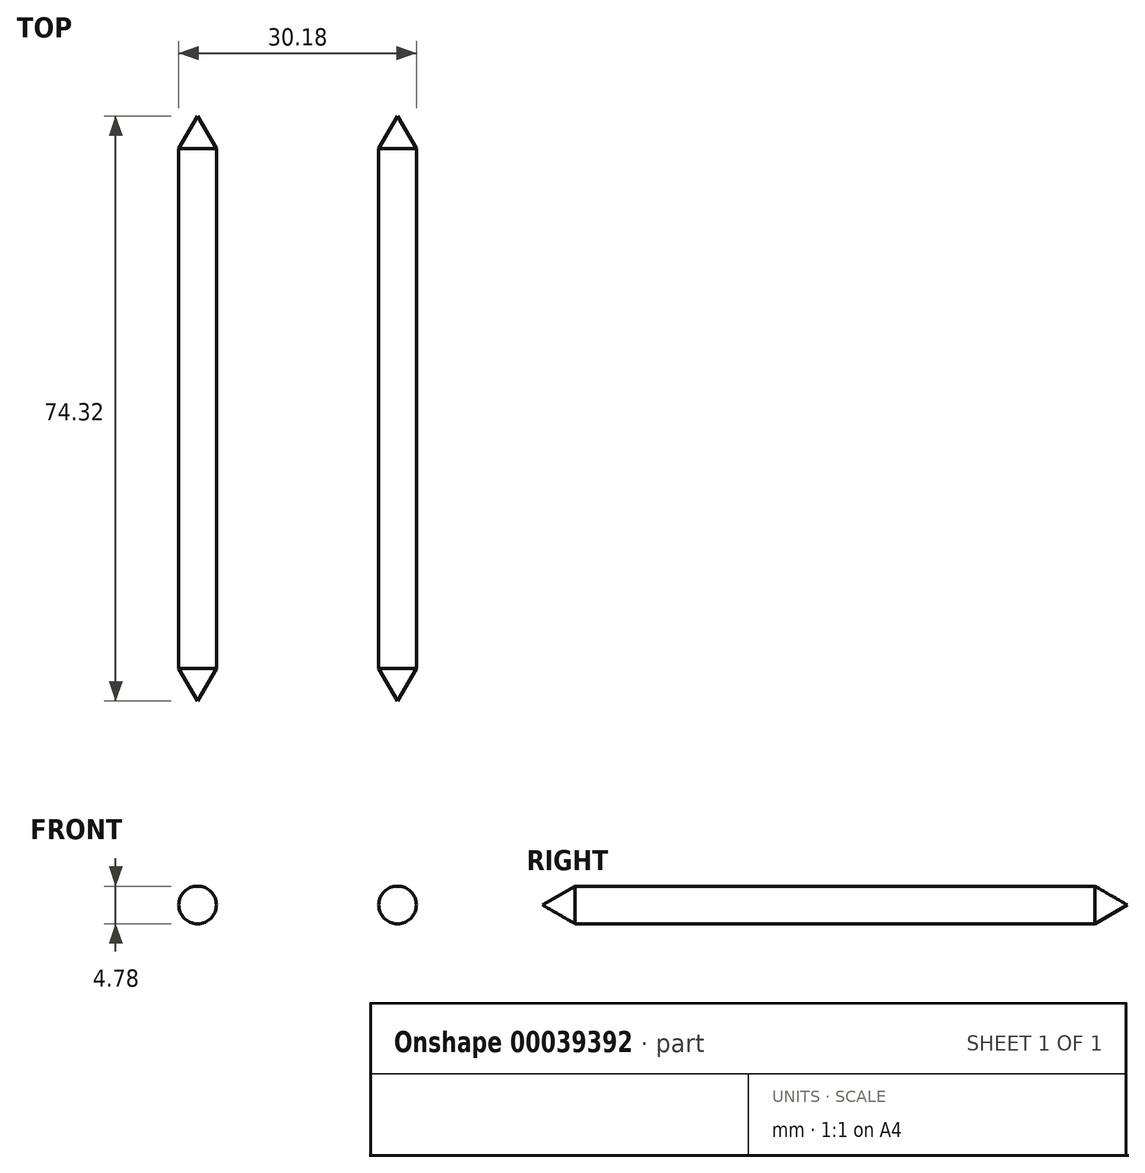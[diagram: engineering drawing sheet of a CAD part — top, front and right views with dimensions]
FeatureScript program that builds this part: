
annotation { "Feature Type Name" : "Feature", "Feature Type Description" : "" }
export const myFeature = defineFeature(function(context is Context, id is Id, definition is map)
    precondition{}
    {
        {
            var Q0;
            Q0=qCreatedBy(makeId("Front.planeOp"),FACE);
            var sketch = newSketch(context, id + "F0", { "sketchPlane" : qUnion([Q0])});
            skCircle(sketch, "E0", {"center": v(0, 0) * mm, "radius": 2.39 * mm});
            skSolve(sketch);
        }
        {
            var Q0;
            Q0 = qSketchRegion(id + "F0", true);
            extrude(context, id + "F1", {"entities" : qUnion([Q0]), "depth" : 66.04 * mm});
        }
        {
            var Q0;
            Q0=makeQuery(id+"F1.opExtrude","CAP_FACE",FACE,{"disambiguationData":[OSD([sQuery(id+"F0.wireOp",EDGE,"E0")])],"isStart":false});
            var sketch = newSketch(context, id + "F2", { "sketchPlane" : qUnion([Q0])});
            skCircle(sketch, "E1", {"center": v(0, 0) * mm, "radius": 2.39 * mm});
            skSolve(sketch);
        }
        {
            var Q0;
            Q0 = qSketchRegion(id + "F2", true);
            extrude(context, id + "F3", {"entities" : qUnion([Q0]), "operationType" : NewBodyOperationType.ADD, "depth" : 12.7 * mm, "hasDraft" : true, "draftAngle" : 30 * degree, "draftPullDirection" : true});
        }
        {
            var Q0;
            Q0=makeQuery(id+"F1.opExtrude","CAP_FACE",FACE,{"disambiguationData":[OSD([sQuery(id+"F0.wireOp",EDGE,"E0")])],"isStart":true});
            var sketch = newSketch(context, id + "F4", { "sketchPlane" : qUnion([Q0])});
            skCircle(sketch, "E2", {"center": v(0, 0) * mm, "radius": 2.39 * mm});
            skSolve(sketch);
        }
        {
            var Q0;
            Q0 = qSketchRegion(id + "F4", true);
            extrude(context, id + "F5", {"entities" : qUnion([Q0]), "operationType" : NewBodyOperationType.ADD, "depth" : 12.7 * mm, "hasDraft" : true, "draftAngle" : 30 * degree, "draftPullDirection" : true});
        }
        {
            var Q0;
            Q0=makeQuery(id+"F1.opExtrude","SWEPT_BODY",BODY,{"disambiguationData":[OSD([sQuery(id+"F0.wireOp",EDGE,"E0")])]});
            transform(context, id + "F6", {"entities" : qUnion([Q0]), "transformType" : TransformType.TRANSLATION_3D, "dx" : 25.4 * mm, "dy" : 0 * mm, "dz" : 0 * mm, "makeCopy" : true});
        }
    });
